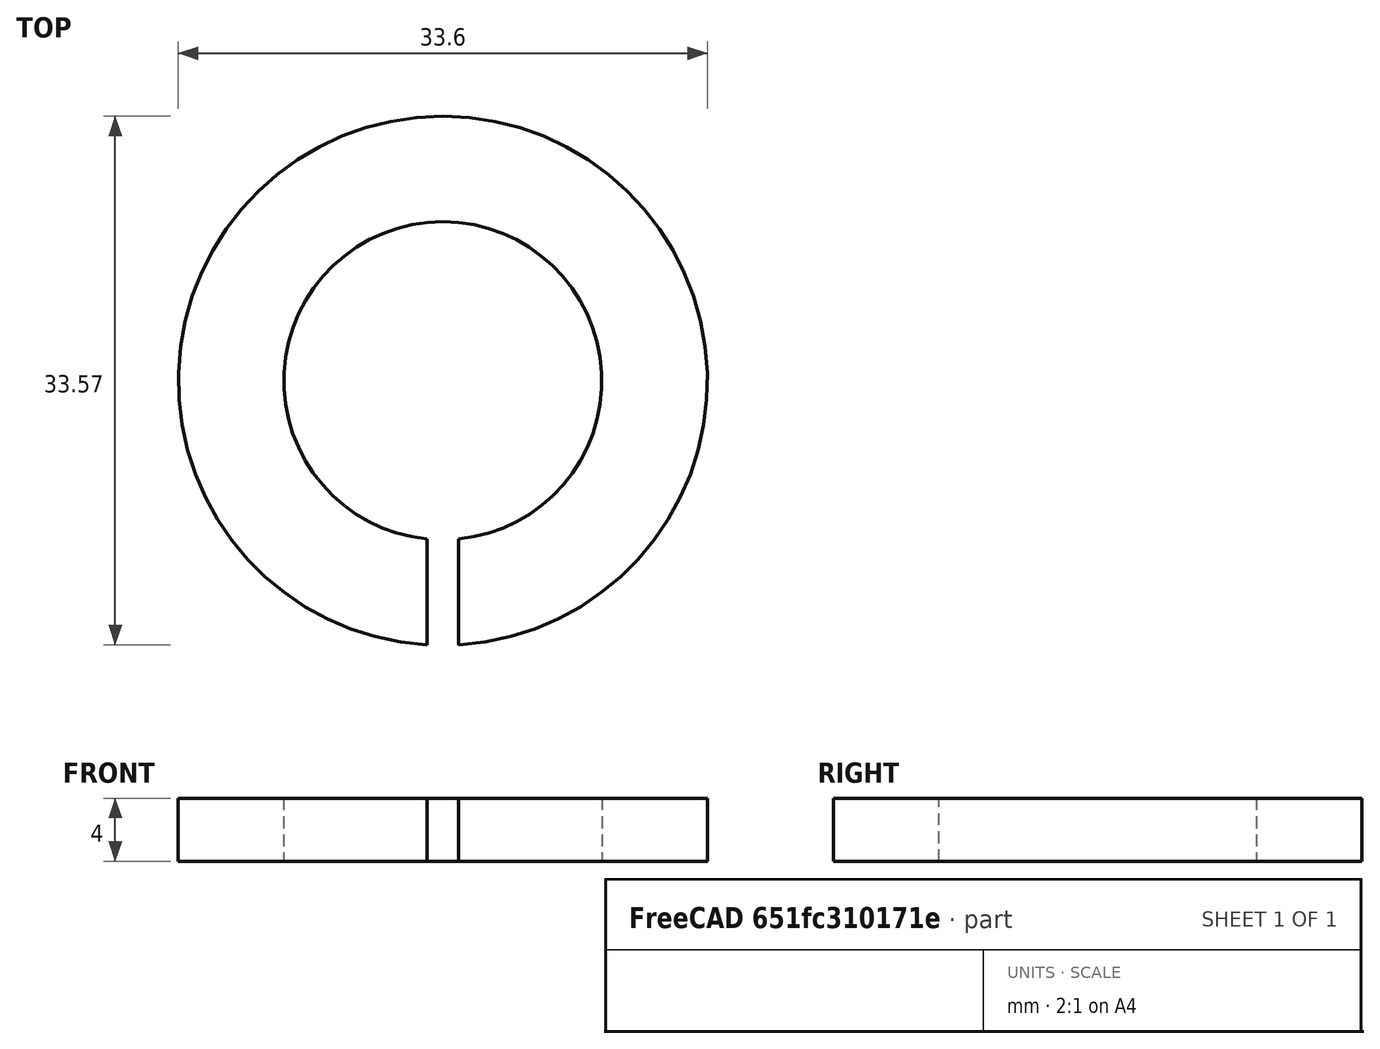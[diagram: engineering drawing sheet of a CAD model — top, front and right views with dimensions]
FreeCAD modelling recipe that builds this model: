
FCSTD DOCUMENT  (FreeCAD 0.15R4651 (Git))
Label: Federring_DIN127-A20
License: All rights reserved
LicenseURL: http://de.wikipedia.org/wiki/Alle_Rechte_vorbehalten
objects: Sketcher::SketchObject×1, PartDesign::Pad×1
note: 3 computed .brp shape members not serialized (recipe doc carries the construction recipe); baked Part::Feature solids carry a one-line shape summary decoded from their .brp

FEATURE [Sketcher::SketchObject] Sketch
  sketch-geometry (4):
    g0: ArcOfCircle CenterX=0 CenterY=0 CenterZ=0 NormalX=0 NormalY=0 NormalZ=1 Radius=10.1 StartAngle=4.81156 EndAngle=10.8964
    g1: ArcOfCircle CenterX=0 CenterY=0 CenterZ=0 NormalX=0 NormalY=0 NormalZ=1 Radius=16.8 StartAngle=4.77195 EndAngle=10.936
    g2: LineSegment StartX=1 StartY=-10.0504 StartZ=0 EndX=1 EndY=-16.7702 EndZ=0
    g3: LineSegment StartX=-1 StartY=-16.7702 StartZ=0 EndX=-1 EndY=-10.0504 EndZ=0
  constraints (12):
    c: Coincident(g0,g-1)
    c: Coincident(g1,g-1)
    c: Vertical(g2)
    c: Vertical(g3)
    c: Coincident(g0,g2)
    c: Coincident(g0,g3)
    c: Coincident(g1,g2)
    c: Coincident(g1,g3)
    c: Symmetric(g1,g1,g-2)
    c: Radius(g0) = 10.1
    c: Radius(g1) = 16.8
    c: DistanceX(g1,g1) = -2
FEATURE [PartDesign::Pad] Pad  label="Federring DIN 127-A 20 #"
  Length = 4
  Length2 = 100
  Midplane = true
  Sketch = -> Sketch
  Type = 0
